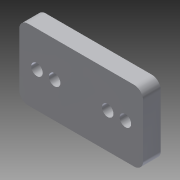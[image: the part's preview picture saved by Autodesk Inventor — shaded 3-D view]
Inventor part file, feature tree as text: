
AUTODESK INVENTOR PART (.ipt)
format: ipt  version: 2014 SP1 (Build 180222100, 222)  size: 100,864 bytes
history: native  units: in
note: dims shown in document units (in); Inventor stores cm internally (conversion verified against a paired STEP export)
features: extrude x1, sketch x1
ambient origin geometry x8: Origin, YZ Plane, XZ Plane, XY Plane, X Axis, Y Axis, Z Axis, Center Point
bodies: Solid1 (feature_tree)
feature tree (2):
  extrude  "Extrusion1"  Depth=1.0in
  sketch  "Sketch1"  dims[d0=1.75in d1=1.0in d2=0.163in d3=0.5in d4=0.25in d5=0.7874in d7=1.0in d8=0.3937in d10=1.0in d21=0.125in d22=0.25in d23=0.0in d25=0.163in d26=0.5in d27=0.25in d28=0.7874in d30=1.0in d31=0.3937in d33=1.0in]
